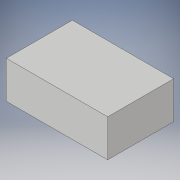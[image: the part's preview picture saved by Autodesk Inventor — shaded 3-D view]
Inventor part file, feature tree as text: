
AUTODESK INVENTOR PART (.ipt)
format: ipt  version: 2018 (Build 220112000, 112)  size: 86,016 bytes
history: native  units: in
note: dims shown in document units (in); Inventor stores cm internally (conversion verified against a paired STEP export)
features: extrude x1, sketch x1
ambient origin geometry x8: Origin, YZ Plane, XZ Plane, XY Plane, X Axis, Y Axis, Z Axis, Center Point
bodies: Solid1 (feature_tree)
feature tree (2):
  extrude  "Extrusion1"  Depth=0.5512in
  sketch  "Sketch1"  dims[d0=0.8465in d1=0.5512in d2=0.311in d3=0.0in]
